# Revit family: PRE050019-FR
name_source: partatom
category: Accessoire de canalisation
revit_build: Autodesk Revit 2017 (Build: 20160225_1515(x64)
units: mm (PartAtom-declared; Revit-internal decimal feet)

## family parameters
Basée sur le plan de construction = Non
Cote de connecteur circulaire = Utiliser le diamètre
Couper avec des vides une fois chargée = Non
Partagée = Non
Toujours verticalement = Oui
Type d'élément = Normal

## types (2) — shared parameters
Adresse = 7, RUE RACINE - 92542 MONTROUGE CEDEX FRANCE
Debit = 8 l/min par limiteur de débit intégré

Brise-jet laminaire

Dispositif anti-coup de bélier
Diamètre Nominal = 15 mm  [stored 0.0492126 ft]
Fabricant = LES ROBINETS PRESTO S.A.
Finition = Corps et Bec en laiton chromé
Flux = 0.1 L/s
Garantie = 3
Hauteur = 250 mm  [stored 0.82021 ft]
LC = 23 mm
Largeur = 45 mm  [stored 0.147638 ft]
Lien CCTP = http://www.prestodatashare.com
Lien fiche produit = http://www.prestodatashare.com
Lien notice d'utilisation = http://www.prestodatashare.com
Matériau = Laiton poli chromé
PC = 23 mm
Perte de charge = 0.0 Pa
Pression = 1 à 5 bars
Profondeur = 182 mm  [stored 0.597113 ft]
Raccordement = Mâle G 1/2" (15x21)
URL = http://www.prestodatashare.com
URL Fabricant = http://www.prestodatashare.com
Variantes = 55450-55451

## per-type parameters (varying)
| type | Description | Fonction | Polantis code | Reference |
| 55451 PRESTO ROBINET SENSAO 6000 SUR PLAGE PILE | Robinet simple sur plage à détection (CE) sur plage. De type Presto SENSAO® réf. 55451 ou techniquement équivalent. Avec cellule optoélectronique, alimentation par pile lithium 6 V dans boîtier déporté IP 65. Limitation de la température maximale par butée réglable, régulateur de débit intégré (8 l/min).Système antiblocage interdisant l'écoulement en continu. Avec  robinet d’arrêt filtre. | Pression d'utilisation recommandée :
- 1 à 5 bars

Débit :
- 8 l/mn par limiteur de débit intégré
- Aérateur anti-tartre haute qualité
- Dispositif anti-coup de bélier

Alimentation hydraulique :
- Mâle G 1/2'' (15x21) en eau froide, chaude ou prémitigée

Alimentation électrique :
- Pile lithium 6 volts type CRP2 dans boîtier déporté

Matière et couleur de finition :
- Corps et bec en laiton chromé
- Bec fixe

Résistance thermique :
- Résiste à une température de 75°C durant 30 minutes dans le cadre de chocs thermiques

Sécurité :
- Fermeture automatique de l'électrovanne en cas d'écoulement > à 30s d'usure de la pile ou de dégradation du détecteur

Livré avec :
- 1 Ecrou de fixation
- 1 Joint et rondelle
- 1 Capillaire, électrovanne 1/2'' (15x21)
- 1 Robinet d'arrêt droit + filtre
- 1 Autocollant de signalisation

Normes / Agréments :
- Laiton conforme aux normes NF EN1982, EN12164, NF EN12165
- Résistant au brouillard salin 200 H (essai NSS) conformément à la norme NF ISO 9227 | PRE050019a-FR | 55451 |
| 55450 PRESTO ROBINET SENSAO 6000 SUR PLAGE SECTEUR | Robinet simple sur plage à détection (CE) sur plage. De type Presto SENSAO® réf. 55450 ou techniquement équivalent. Avec cellule optoélectronique, alimentation secteur par transformateur 230/7 Volt déporté dans boîtier étanche IP65. Limitation de la température maximale par butée réglable, régulateur de débit intégré (8 l/min).Système antiblocage interdisant l'écoulement en continu. Avec  robinet d’arrêt filtre. | Pression d'utilisation recommandée :
- 1 à 5 bars

Débit :
- 8 l/mn par limiteur de débit intégré
- Aérateur anti-tartre haute qualité
- Dispositif anti-coup de bélier

Alimentation hydraulique :
- Mâle G 1/2'' (15x21) en eau froide, chaude ou prémitigée

Alimentation électrique :
- Avec transformateur 230 Vac / 7 Vdc dans boîtier étanche IP65

Matière et couleur de finition :
- Corps et bec en laiton chromé
- Bec fixe

Résistance thermique :
- Résiste à une température de 75°C durant 30 minutes dans le cadre de chocs thermiques

Sécurité :
- Fermeture automatique de l'électrovanne en cas d'écoulement > à 30s ou de dégradation du détecteur

Livré avec :
- 1 Ecrou de fixation
- 1 Joint et rondelle
- 1 Capillaire, électrovanne 1/2'' (15x21)
- 1 Robinet d'arrêt droit + filtre
- 1 Autocollant de signalisation

Normes / Agréments :
- Laiton conforme aux normes NF EN1982, EN12164, NF EN12165
- Résistant au brouillard salin 200 H (essai NSS) conformément à la norme NF ISO 9227 | PRE050019-FR | 55450 |

note: column(s) folded — value = type name in every type: Modèle

note: [stored X ft] marks values corroborated as IEEE doubles in the binary element streams (Revit-internal decimal feet)
